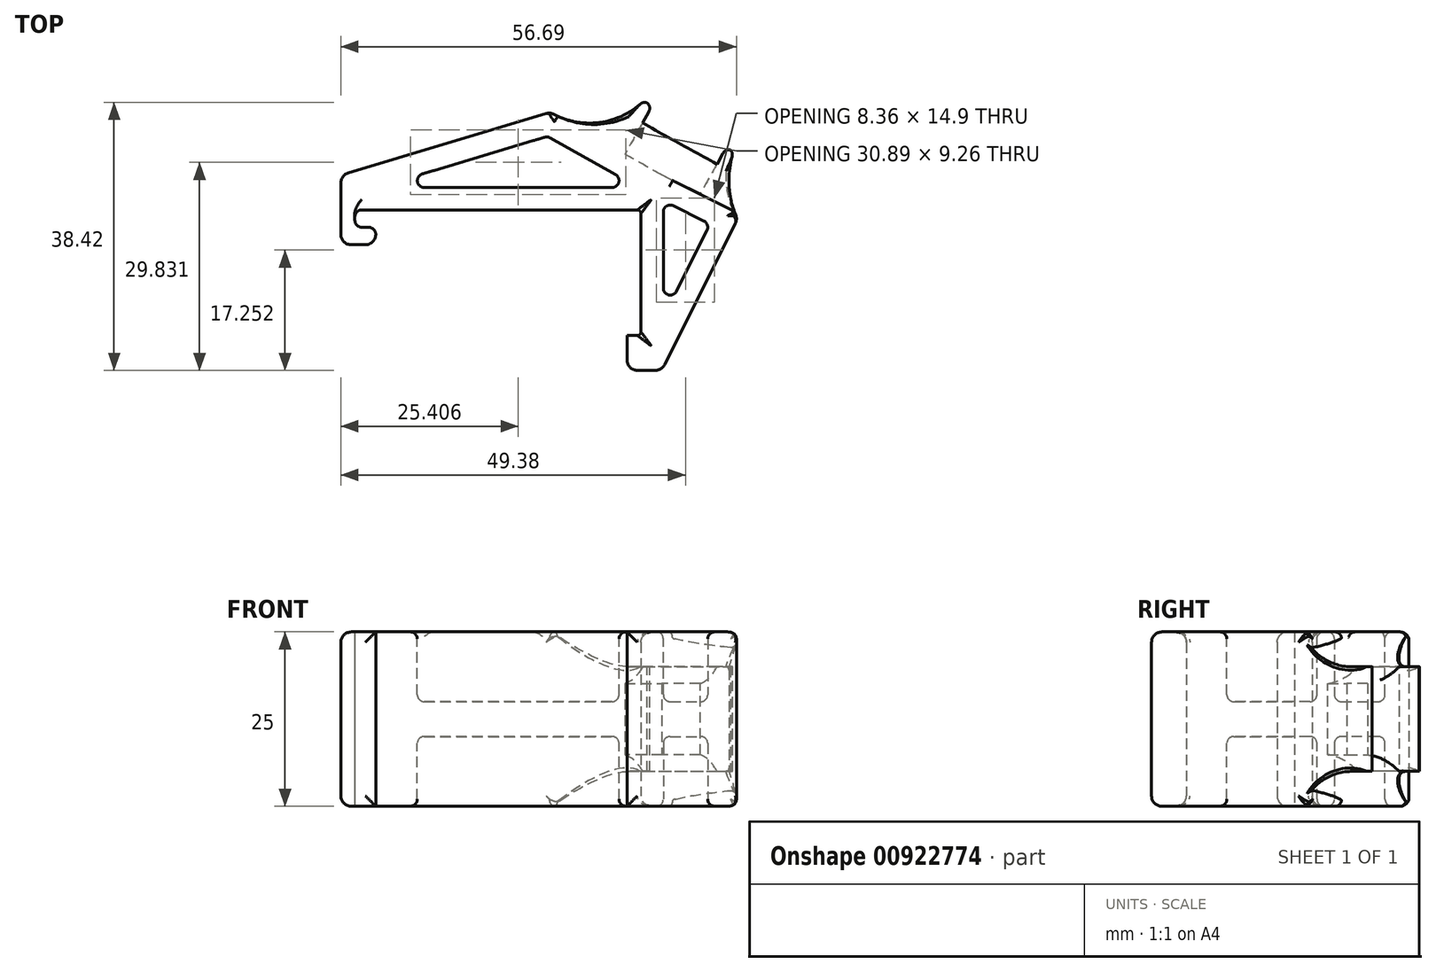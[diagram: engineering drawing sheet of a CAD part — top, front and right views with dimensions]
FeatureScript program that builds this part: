
annotation { "Feature Type Name" : "Feature", "Feature Type Description" : "" }
export const myFeature = defineFeature(function(context is Context, id is Id, definition is map)
    precondition{}
    {
        {
            var Q0;
            Q0=qCreatedBy(makeId("Top.planeOp"),FACE);
            var sketch = newSketch(context, id + "F0", { "sketchPlane" : qUnion([Q0])});
            skLineSegment(sketch, "E0.bottom", {"start": v(0, 0) * mm, "end": v(41, 0) * mm});
            skLineSegment(sketch, "E0.top", {"start": v(0, 2) * mm, "end": v(41, 2) * mm});
            skLineSegment(sketch, "E0.left", {"start": v(0, 0) * mm, "end": v(0, 2) * mm});
            skLineSegment(sketch, "E0.right", {"start": v(41, 0) * mm, "end": v(41, 2) * mm});
            skLineSegment(sketch, "E1.bottom", {"start": v(0, 2) * mm, "end": v(-2, 2) * mm});
            skLineSegment(sketch, "E1.top", {"start": v(0, -2.5) * mm, "end": v(-2, -2.5) * mm});
            skLineSegment(sketch, "E1.left", {"start": v(0, 2) * mm, "end": v(0, -2.5) * mm});
            skLineSegment(sketch, "E1.right", {"start": v(-2, 2) * mm, "end": v(-2, -2.5) * mm});
            skLineSegment(sketch, "E2.bottom", {"start": v(-2, -2.5) * mm, "end": v(3, -2.5) * mm});
            skLineSegment(sketch, "E2.top", {"start": v(-2, -5) * mm, "end": v(3, -5) * mm});
            skLineSegment(sketch, "E2.left", {"start": v(-2, -2.5) * mm, "end": v(-2, -5) * mm});
            skLineSegment(sketch, "E2.right", {"start": v(3, -2.5) * mm, "end": v(3, -5) * mm});
            skLineSegment(sketch, "E3.bottom", {"start": v(41, 2) * mm, "end": v(44, 2) * mm});
            skLineSegment(sketch, "E3.top", {"start": v(41, -23) * mm, "end": v(44, -23) * mm});
            skLineSegment(sketch, "E3.left", {"start": v(41, 2) * mm, "end": v(41, -23) * mm});
            skLineSegment(sketch, "E3.right", {"start": v(44, 2) * mm, "end": v(44, -23) * mm});
            skLineSegment(sketch, "E4.bottom", {"start": v(41, -23) * mm, "end": v(39, -23) * mm});
            skLineSegment(sketch, "E4.top", {"start": v(41, -18) * mm, "end": v(39, -18) * mm});
            skLineSegment(sketch, "E4.left", {"start": v(41, -23) * mm, "end": v(41, -18) * mm});
            skLineSegment(sketch, "E4.right", {"start": v(39, -23) * mm, "end": v(39, -18) * mm});
            skLineSegment(sketch, "E5.bottom", {"start": v(39, -23) * mm, "end": v(37.5, -23) * mm});
            skLineSegment(sketch, "E5.top", {"start": v(39, -13) * mm, "end": v(37.5, -13) * mm});
            skLineSegment(sketch, "E5.left", {"start": v(39, -23) * mm, "end": v(39, -13) * mm});
            skLineSegment(sketch, "E5.right", {"start": v(37.5, -23) * mm, "end": v(37.5, -13) * mm});
            skLineSegment(sketch, "E6.bottom", {"start": v(-2, 2) * mm, "end": v(44, 2) * mm});
            skLineSegment(sketch, "E6.top", {"start": v(-2, 5) * mm, "end": v(44, 5) * mm});
            skLineSegment(sketch, "E6.left", {"start": v(-2, 2) * mm, "end": v(-2, 5) * mm});
            skLineSegment(sketch, "E6.right", {"start": v(44, 2) * mm, "end": v(44, 5) * mm});
            skLineSegment(sketch, "E7", {"start": v(44, 5) * mm, "end": v(28, 14) * mm});
            skLineSegment(sketch, "E8", {"start": v(28, 14) * mm, "end": v(-2, 5) * mm});
            skLineSegment(sketch, "E9", {"start": v(28, 14) * mm, "end": v(28, 5) * mm});
            skLineSegment(sketch, "E10.bottom", {"start": v(37.5, -23) * mm, "end": v(39, -23) * mm});
            skLineSegment(sketch, "E10.top", {"start": v(37.5, -18) * mm, "end": v(39, -18) * mm});
            skLineSegment(sketch, "E10.left", {"start": v(37.5, -23) * mm, "end": v(37.5, -18) * mm});
            skLineSegment(sketch, "E11.bottom", {"start": v(44, 5) * mm, "end": v(28, 5) * mm});
            skLineSegment(sketch, "E11.top", {"start": v(44, 14) * mm, "end": v(28, 14) * mm});
            skLineSegment(sketch, "E11.left", {"start": v(44, 5) * mm, "end": v(44, 14) * mm});
            skLineSegment(sketch, "E11.right", {"start": v(28, 5) * mm, "end": v(28, 14) * mm});
            skLineSegment(sketch, "E12.bottom", {"start": v(-2, 5) * mm, "end": v(28, 5) * mm});
            skLineSegment(sketch, "E12.top", {"start": v(-2, 14) * mm, "end": v(28, 14) * mm});
            skLineSegment(sketch, "E12.left", {"start": v(-2, 5) * mm, "end": v(-2, 14) * mm});
            skLineSegment(sketch, "E13.bottom", {"start": v(44, 5) * mm, "end": v(62, 5) * mm});
            skLineSegment(sketch, "E13.top", {"start": v(44, -4) * mm, "end": v(62, -4) * mm});
            skLineSegment(sketch, "E13.left", {"start": v(44, 5) * mm, "end": v(44, -4) * mm});
            skLineSegment(sketch, "E13.right", {"start": v(62, 5) * mm, "end": v(62, -4) * mm});
            skLineSegment(sketch, "E14", {"start": v(44, 5) * mm, "end": v(62, -4) * mm});
            skLineSegment(sketch, "E15", {"start": v(62, -4) * mm, "end": v(44, -23) * mm});
            skLineSegment(sketch, "E16", {"start": v(44, -23) * mm, "end": v(55.2, -0.6) * mm});
            skSolve(sketch);
        }
        {
            var Q0;
            Q0=makeQuery(id+"F0.imprint","IMPRINT",FACE,{"disambiguationData":[TD([[makeQuery(id+"F0.imprint","IMPRINT",EDGE,{"derivedFrom":sQuery(id+"F0.wireOp",EDGE,"E2.top")}),1.0]])]});
            var Q1;
            Q1=makeQuery(id+"F0.imprint","IMPRINT",FACE,{"disambiguationData":[TD([[makeQuery(id+"F0.imprint","IMPRINT",EDGE,{"derivedFrom":sQuery(id+"F0.wireOp",EDGE,"E4.bottom")}),-1.0]])]});
            var Q2;
            Q2=makeQuery(id+"F0.imprint","IMPRINT",FACE,{"disambiguationData":[TD([[makeQuery(id+"F0.imprint","IMPRINT",EDGE,{"derivedFrom":sQuery(id+"F0.wireOp",EDGE,"E10.bottom")}),1.0]])]});
            var Q3;
            {var subQ0=sQuery(id+"F0.wireOp",EDGE,"E6.left");Q3=makeQuery(id+"F0.imprint","IMPRINT",FACE,{"disambiguationData":[TD([[makeQuery(id+"F0.imprint","IMPRINT",EDGE,{"derivedFrom":subQ0}),-1.0]])]});}
            var Q4;
            Q4=makeQuery(id+"F0.imprint","IMPRINT",FACE,{"disambiguationData":[TD([[makeQuery(id+"F0.imprint","IMPRINT",EDGE,{"derivedFrom":sQuery(id+"F0.wireOp",EDGE,"E3.right")}),1.0]])]});
            var Q5;
            Q5=makeQuery(id+"F0.imprint","IMPRINT",FACE,{"disambiguationData":[TD([[makeQuery(id+"F0.imprint","IMPRINT",EDGE,{"derivedFrom":sQuery(id+"F0.wireOp",EDGE,"E3.top")}),1.0]])]});
            var Q6;
            {var subQ4=sQuery(id+"F0.wireOp",EDGE,"E14");var subQ6=sQuery(id+"F0.wireOp",EDGE,"E16");var subQ7=makeQuery(id+"F0.imprint","INTERSECT",VERTEX,{"derivedFrom":[subQ4,subQ6]});Q6=makeQuery(id+"F0.imprint","IMPRINT",FACE,{"disambiguationData":[TD([[makeQuery(id+"F0.imprint","IMPRINT",EDGE,{"disambiguationData":[TD([[subQ7,1.0]])],"derivedFrom":subQ6}),1.0]])]});}
            var Q7;
            Q7=makeQuery(id+"F0.imprint","IMPRINT",FACE,{"disambiguationData":[TD([[makeQuery(id+"F0.imprint","IMPRINT",EDGE,{"derivedFrom":sQuery(id+"F0.wireOp",EDGE,"E8")}),1.0]])]});
            var Q8;
            {var subQ3=sQuery(id+"F0.wireOp",EDGE,"E1.right");Q8=makeQuery(id+"F0.imprint","IMPRINT",FACE,{"disambiguationData":[TD([[makeQuery(id+"F0.imprint","IMPRINT",EDGE,{"derivedFrom":subQ3}),1.0]])]});}
            var Q9;
            Q9=makeQuery(id+"F0.imprint","IMPRINT",FACE,{"disambiguationData":[TD([[makeQuery(id+"F0.imprint","IMPRINT",EDGE,{"derivedFrom":sQuery(id+"F0.wireOp",EDGE,"E7")}),1.0]])]});
            var Q10;
            {var subQ0=sQuery(id+"F0.wireOp",EDGE,"E0.bottom");Q10=makeQuery(id+"F0.imprint","IMPRINT",FACE,{"disambiguationData":[TD([[makeQuery(id+"F0.imprint","IMPRINT",EDGE,{"derivedFrom":subQ0}),1.0]])]});}
            extrude(context, id + "F1", {"entities" : qUnion([Q0, Q1, Q2, Q3, Q4, Q5, Q6, Q7, Q8, Q9, Q10]), "depth" : 12.5 * mm, "offsetDistance" : 25 * mm, "hasSecondDirection" : true, "secondDirectionOppositeDirection" : true, "secondDirectionDepth" : 12.5 * mm});
        }
        {
            var Q0;
            Q0=makeQuery(id+"F1.opExtrude","CAP_FACE",FACE,{"disambiguationData":[OSD([sQuery(id+"F0.wireOp",EDGE,"E1.left"),sQuery(id+"F0.wireOp",EDGE,"E1.right"),sQuery(id+"F0.wireOp",EDGE,"E2.bottom"),sQuery(id+"F0.wireOp",EDGE,"E2.top"),sQuery(id+"F0.wireOp",EDGE,"E2.left"),sQuery(id+"F0.wireOp",EDGE,"E2.right"),sQuery(id+"F0.wireOp",EDGE,"E3.top"),sQuery(id+"F0.wireOp",EDGE,"E3.left"),sQuery(id+"F0.wireOp",EDGE,"E4.bottom"),sQuery(id+"F0.wireOp",EDGE,"E4.top"),sQuery(id+"F0.wireOp",EDGE,"E6.bottom"),sQuery(id+"F0.wireOp",EDGE,"E6.left"),sQuery(id+"F0.wireOp",EDGE,"E7"),sQuery(id+"F0.wireOp",EDGE,"E8"),sQuery(id+"F0.wireOp",EDGE,"E10.bottom"),sQuery(id+"F0.wireOp",EDGE,"E10.top"),sQuery(id+"F0.wireOp",EDGE,"E10.left"),sQuery(id+"F0.wireOp",EDGE,"E14"),sQuery(id+"F0.wireOp",EDGE,"E16")])],"isStart":false});
            var Q1;
            Q1=makeQuery(id+"F1.opExtrude","CAP_FACE",FACE,{"disambiguationData":[OSD([sQuery(id+"F0.wireOp",EDGE,"E1.left"),sQuery(id+"F0.wireOp",EDGE,"E1.right"),sQuery(id+"F0.wireOp",EDGE,"E2.bottom"),sQuery(id+"F0.wireOp",EDGE,"E2.top"),sQuery(id+"F0.wireOp",EDGE,"E2.left"),sQuery(id+"F0.wireOp",EDGE,"E2.right"),sQuery(id+"F0.wireOp",EDGE,"E3.top"),sQuery(id+"F0.wireOp",EDGE,"E3.left"),sQuery(id+"F0.wireOp",EDGE,"E4.bottom"),sQuery(id+"F0.wireOp",EDGE,"E4.top"),sQuery(id+"F0.wireOp",EDGE,"E6.bottom"),sQuery(id+"F0.wireOp",EDGE,"E6.left"),sQuery(id+"F0.wireOp",EDGE,"E7"),sQuery(id+"F0.wireOp",EDGE,"E8"),sQuery(id+"F0.wireOp",EDGE,"E10.bottom"),sQuery(id+"F0.wireOp",EDGE,"E10.top"),sQuery(id+"F0.wireOp",EDGE,"E10.left"),sQuery(id+"F0.wireOp",EDGE,"E14"),sQuery(id+"F0.wireOp",EDGE,"E16")])],"isStart":true});
            shell(context, id + "F2", {"entities" : qUnion([Q0, Q1]), "thickness" : 3.2 * mm});
        }
        {
            var Q0;
            Q0=makeQuery(id+"F1.opExtrude","SWEPT_FACE",FACE,{"disambiguationData":[OSD([sQuery(id+"F0.wireOp",EDGE,"E7"),sQuery(id+"F0.wireOp",EDGE,"E14")])]});
            var sketch = newSketch(context, id + "F3", { "sketchPlane" : qUnion([Q0])});
            skLineSegment(sketch, "E17", {"start": v(-17.54, 0) * mm, "end": v(-48.4, 0) * mm});
            skLineSegment(sketch, "E18", {"start": v(-35.9, 0) * mm, "end": v(-35.9, 12.5) * mm});
            skLineSegment(sketch, "E19.bottom", {"start": v(-29.8, 5.1) * mm, "end": v(-42, 5.1) * mm});
            skLineSegment(sketch, "E19.top", {"start": v(-29.8, -5.1) * mm, "end": v(-42, -5.1) * mm});
            skLineSegment(sketch, "E19.left", {"start": v(-29.8, 5.1) * mm, "end": v(-29.8, -5.1) * mm});
            skLineSegment(sketch, "E19.right", {"start": v(-42, 5.1) * mm, "end": v(-42, -5.1) * mm});
            skPoint(sketch, "E19.middle", {"position": v(-35.9, 0) * mm});
            skLineSegment(sketch, "E20.bottom", {"start": v(-28.4, 7.5) * mm, "end": v(-43.4, 7.5) * mm});
            skLineSegment(sketch, "E20.top", {"start": v(-28.4, -7.5) * mm, "end": v(-43.4, -7.5) * mm});
            skLineSegment(sketch, "E20.left", {"start": v(-28.4, 7.5) * mm, "end": v(-28.4, -7.5) * mm});
            skLineSegment(sketch, "E20.right", {"start": v(-43.4, 7.5) * mm, "end": v(-43.4, -7.5) * mm});
            skSolve(sketch);
        }
        {
            var Q0;
            Q0 = qSketchRegion(id + "F3", true);
            extrude(context, id + "F4", {"entities" : qUnion([Q0]), "operationType" : NewBodyOperationType.ADD, "depth" : 8 * mm, "offsetDistance" : 25 * mm});
        }
        {
            var Q0;
            Q0=makeQuery(id+"F4.opExtrude","CAP_EDGE",EDGE,{"disambiguationData":[OSD([sQuery(id+"F3.wireOp",EDGE,"E19.bottom")])],"isStart":false});
            var Q1;
            Q1=makeQuery(id+"F4.opExtrude","CAP_EDGE",EDGE,{"disambiguationData":[OSD([sQuery(id+"F3.wireOp",EDGE,"E19.top")])],"isStart":false});
            fillet(context, id + "F5", {"entities" : qUnion([Q0, Q1]), "radius" : 9 * mm, "tangentPropagation" : true, "allowEdgeOverflow" : false});
        }
        {
            var Q0;
            Q0=makeQuery(id+"F4.opExtrude","CAP_EDGE",EDGE,{"disambiguationData":[OSD([sQuery(id+"F3.wireOp",EDGE,"E20.bottom")])],"isStart":true});
            var Q1;
            Q1=makeQuery(id+"F4.opExtrude","CAP_EDGE",EDGE,{"disambiguationData":[OSD([sQuery(id+"F3.wireOp",EDGE,"E20.top")])],"isStart":true});
            var Q2;
            Q2=makeQuery(id+"F4.opExtrude","CAP_EDGE",EDGE,{"disambiguationData":[OSD([sQuery(id+"F3.wireOp",EDGE,"E20.right")])],"isStart":true});
            fillet(context, id + "F6", {"entities" : qUnion([Q0, Q1, Q2]), "radius" : 5 * mm, "tangentPropagation" : true, "allowEdgeOverflow" : false});
        }
        {
            var Q0;
            Q0=makeQuery(id+"F4.opExtrude","CAP_EDGE",EDGE,{"disambiguationData":[OSD([sQuery(id+"F3.wireOp",EDGE,"E20.left")])],"isStart":true});
            fillet(context, id + "F7", {"entities" : qUnion([Q0]), "radius" : 11 * mm, "tangentPropagation" : true, "allowEdgeOverflow" : false});
        }
        {
            var Q0;
            {var subQ0=sQuery(id+"F0.wireOp",EDGE,"E6.left");Q0=makeQuery(id+"F0.imprint","IMPRINT",FACE,{"disambiguationData":[TD([[makeQuery(id+"F0.imprint","IMPRINT",EDGE,{"derivedFrom":subQ0}),-1.0]])]});}
            var Q1;
            Q1=makeQuery(id+"F0.imprint","IMPRINT",FACE,{"disambiguationData":[TD([[makeQuery(id+"F0.imprint","IMPRINT",EDGE,{"derivedFrom":sQuery(id+"F0.wireOp",EDGE,"E7")}),1.0]])]});
            var Q2;
            Q2=makeQuery(id+"F0.imprint","IMPRINT",FACE,{"disambiguationData":[TD([[makeQuery(id+"F0.imprint","IMPRINT",EDGE,{"derivedFrom":sQuery(id+"F0.wireOp",EDGE,"E8")}),1.0]])]});
            var Q3;
            {var subQ4=sQuery(id+"F0.wireOp",EDGE,"E14");var subQ6=sQuery(id+"F0.wireOp",EDGE,"E16");var subQ7=makeQuery(id+"F0.imprint","INTERSECT",VERTEX,{"derivedFrom":[subQ4,subQ6]});Q3=makeQuery(id+"F0.imprint","IMPRINT",FACE,{"disambiguationData":[TD([[makeQuery(id+"F0.imprint","IMPRINT",EDGE,{"disambiguationData":[TD([[subQ7,1.0]])],"derivedFrom":subQ6}),1.0]])]});}
            var Q4;
            {var subQ0=sQuery(id+"F0.wireOp",EDGE,"E3.right");Q4=makeQuery(id+"F0.imprint","IMPRINT",FACE,{"disambiguationData":[TD([[makeQuery(id+"F0.imprint","IMPRINT",EDGE,{"derivedFrom":subQ0}),1.0]])]});}
            extrude(context, id + "F8", {"entities" : qUnion([Q0, Q1, Q2, Q3, Q4]), "operationType" : NewBodyOperationType.ADD, "depth" : 2.5 * mm, "offsetDistance" : 25 * mm, "hasSecondDirection" : true, "secondDirectionOppositeDirection" : true, "secondDirectionDepth" : 2.5 * mm});
        }
        {
            var Q0;
            Q0=makeQuery(id+"F1.opExtrude","SWEPT_FACE",FACE,{"disambiguationData":[OSD([sQuery(id+"F0.wireOp",EDGE,"E1.right"),sQuery(id+"F0.wireOp",EDGE,"E2.left"),sQuery(id+"F0.wireOp",EDGE,"E6.left")])]});
            var Q1;
            Q1=makeQuery(id+"F1.opExtrude","SWEPT_FACE",FACE,{"disambiguationData":[OSD([sQuery(id+"F0.wireOp",EDGE,"E2.top")])]});
            var Q2;
            Q2=makeQuery(id+"F1.opExtrude","SWEPT_FACE",FACE,{"disambiguationData":[OSD([sQuery(id+"F0.wireOp",EDGE,"E8")])]});
            var Q3;
            Q3=makeQuery(id+"F1.opExtrude","SWEPT_FACE",FACE,{"disambiguationData":[OSD([sQuery(id+"F0.wireOp",EDGE,"E16")])]});
            var Q4;
            Q4=makeQuery(id+"F1.opExtrude","SWEPT_FACE",FACE,{"disambiguationData":[OSD([sQuery(id+"F0.wireOp",EDGE,"E3.top"),sQuery(id+"F0.wireOp",EDGE,"E4.bottom"),sQuery(id+"F0.wireOp",EDGE,"E10.bottom")])]});
            var Q5;
            Q5=makeQuery(id+"F1.opExtrude","SWEPT_FACE",FACE,{"disambiguationData":[OSD([sQuery(id+"F0.wireOp",EDGE,"E10.left")])]});
            var Q6;
            Q6=makeQuery(id+"F1.opExtrude","CAP_EDGE",EDGE,{"disambiguationData":[OSD([sQuery(id+"F0.wireOp",EDGE,"E4.top"),sQuery(id+"F0.wireOp",EDGE,"E10.top")])],"isStart":false});
            var Q7;
            Q7=makeQuery(id+"F1.opExtrude","CAP_EDGE",EDGE,{"disambiguationData":[OSD([sQuery(id+"F0.wireOp",EDGE,"E3.left")])],"isStart":false});
            var Q8;
            Q8=makeQuery(id+"F1.opExtrude","CAP_EDGE",EDGE,{"disambiguationData":[OSD([sQuery(id+"F0.wireOp",EDGE,"E0.bottom")])],"isStart":false});
            var Q9;
            Q9=makeQuery(id+"F1.opExtrude","CAP_EDGE",EDGE,{"disambiguationData":[OSD([sQuery(id+"F0.wireOp",EDGE,"E4.top"),sQuery(id+"F0.wireOp",EDGE,"E10.top")])],"isStart":true});
            var Q10;
            Q10=makeQuery(id+"F1.opExtrude","CAP_EDGE",EDGE,{"disambiguationData":[OSD([sQuery(id+"F0.wireOp",EDGE,"E3.left")])],"isStart":true});
            var Q11;
            Q11=makeQuery(id+"F1.opExtrude","CAP_EDGE",EDGE,{"disambiguationData":[OSD([sQuery(id+"F0.wireOp",EDGE,"E0.bottom")])],"isStart":true});
            fillet(context, id + "F9", {"entities" : qUnion([Q0, Q1, Q2, Q3, Q4, Q5, Q6, Q7, Q8, Q9, Q10, Q11]), "radius" : 1.5 * mm, "tangentPropagation" : true, "allowEdgeOverflow" : false});
        }
        {
            var Q0;
            {var subQ0=sQuery(id+"F0.wireOp",EDGE,"E14");var subQ1=sQuery(id+"F0.wireOp",EDGE,"E7");Q0=makeQuery(id+"F7.opFillet","MERGE",EDGE,{"derivedFrom":[makeQuery(id+"F6.opFillet","BLEND_EDGE",EDGE,{"blendedFrom":[makeQuery(id+"F4.opExtrude","CAP_EDGE",EDGE,{"disambiguationData":[OSD([sQuery(id+"F3.wireOp",EDGE,"E20.top")])],"isStart":true}),makeQuery(id+"F1.opExtrude","CAP_FACE",FACE,{"disambiguationData":[OSD([sQuery(id+"F0.wireOp",EDGE,"E1.left"),sQuery(id+"F0.wireOp",EDGE,"E1.right"),sQuery(id+"F0.wireOp",EDGE,"E2.bottom"),sQuery(id+"F0.wireOp",EDGE,"E2.top"),sQuery(id+"F0.wireOp",EDGE,"E2.left"),sQuery(id+"F0.wireOp",EDGE,"E2.right"),sQuery(id+"F0.wireOp",EDGE,"E3.top"),sQuery(id+"F0.wireOp",EDGE,"E3.left"),sQuery(id+"F0.wireOp",EDGE,"E4.bottom"),sQuery(id+"F0.wireOp",EDGE,"E4.top"),sQuery(id+"F0.wireOp",EDGE,"E6.bottom"),sQuery(id+"F0.wireOp",EDGE,"E6.left"),subQ1,sQuery(id+"F0.wireOp",EDGE,"E8"),sQuery(id+"F0.wireOp",EDGE,"E10.bottom"),sQuery(id+"F0.wireOp",EDGE,"E10.top"),sQuery(id+"F0.wireOp",EDGE,"E10.left"),subQ0,sQuery(id+"F0.wireOp",EDGE,"E16")])],"isStart":true})],"blendedInto":[makeQuery(id+"F1.opExtrude","CAP_FACE",FACE,{"disambiguationData":[OSD([sQuery(id+"F0.wireOp",EDGE,"E1.left"),sQuery(id+"F0.wireOp",EDGE,"E1.right"),sQuery(id+"F0.wireOp",EDGE,"E2.bottom"),sQuery(id+"F0.wireOp",EDGE,"E2.top"),sQuery(id+"F0.wireOp",EDGE,"E2.left"),sQuery(id+"F0.wireOp",EDGE,"E2.right"),sQuery(id+"F0.wireOp",EDGE,"E3.top"),sQuery(id+"F0.wireOp",EDGE,"E3.left"),sQuery(id+"F0.wireOp",EDGE,"E4.bottom"),sQuery(id+"F0.wireOp",EDGE,"E4.top"),sQuery(id+"F0.wireOp",EDGE,"E6.bottom"),sQuery(id+"F0.wireOp",EDGE,"E6.left"),subQ1,sQuery(id+"F0.wireOp",EDGE,"E8"),sQuery(id+"F0.wireOp",EDGE,"E10.bottom"),sQuery(id+"F0.wireOp",EDGE,"E10.top"),sQuery(id+"F0.wireOp",EDGE,"E10.left"),subQ0,sQuery(id+"F0.wireOp",EDGE,"E16")])],"isStart":true})]}),makeQuery(id+"F1.opExtrude","CAP_EDGE",EDGE,{"disambiguationData":[OSD([subQ1,subQ0])],"isStart":true})]});}
            var Q1;
            {var subQ0=sQuery(id+"F0.wireOp",EDGE,"E14");var subQ1=sQuery(id+"F0.wireOp",EDGE,"E7");Q1=makeQuery(id+"F7.opFillet","MERGE",EDGE,{"derivedFrom":[makeQuery(id+"F6.opFillet","BLEND_EDGE",EDGE,{"blendedFrom":[makeQuery(id+"F4.opExtrude","CAP_EDGE",EDGE,{"disambiguationData":[OSD([sQuery(id+"F3.wireOp",EDGE,"E20.bottom")])],"isStart":true}),makeQuery(id+"F1.opExtrude","CAP_FACE",FACE,{"disambiguationData":[OSD([sQuery(id+"F0.wireOp",EDGE,"E1.left"),sQuery(id+"F0.wireOp",EDGE,"E1.right"),sQuery(id+"F0.wireOp",EDGE,"E2.bottom"),sQuery(id+"F0.wireOp",EDGE,"E2.top"),sQuery(id+"F0.wireOp",EDGE,"E2.left"),sQuery(id+"F0.wireOp",EDGE,"E2.right"),sQuery(id+"F0.wireOp",EDGE,"E3.top"),sQuery(id+"F0.wireOp",EDGE,"E3.left"),sQuery(id+"F0.wireOp",EDGE,"E4.bottom"),sQuery(id+"F0.wireOp",EDGE,"E4.top"),sQuery(id+"F0.wireOp",EDGE,"E6.bottom"),sQuery(id+"F0.wireOp",EDGE,"E6.left"),subQ1,sQuery(id+"F0.wireOp",EDGE,"E8"),sQuery(id+"F0.wireOp",EDGE,"E10.bottom"),sQuery(id+"F0.wireOp",EDGE,"E10.top"),sQuery(id+"F0.wireOp",EDGE,"E10.left"),subQ0,sQuery(id+"F0.wireOp",EDGE,"E16")])],"isStart":false})],"blendedInto":[makeQuery(id+"F1.opExtrude","CAP_FACE",FACE,{"disambiguationData":[OSD([sQuery(id+"F0.wireOp",EDGE,"E1.left"),sQuery(id+"F0.wireOp",EDGE,"E1.right"),sQuery(id+"F0.wireOp",EDGE,"E2.bottom"),sQuery(id+"F0.wireOp",EDGE,"E2.top"),sQuery(id+"F0.wireOp",EDGE,"E2.left"),sQuery(id+"F0.wireOp",EDGE,"E2.right"),sQuery(id+"F0.wireOp",EDGE,"E3.top"),sQuery(id+"F0.wireOp",EDGE,"E3.left"),sQuery(id+"F0.wireOp",EDGE,"E4.bottom"),sQuery(id+"F0.wireOp",EDGE,"E4.top"),sQuery(id+"F0.wireOp",EDGE,"E6.bottom"),sQuery(id+"F0.wireOp",EDGE,"E6.left"),subQ1,sQuery(id+"F0.wireOp",EDGE,"E8"),sQuery(id+"F0.wireOp",EDGE,"E10.bottom"),sQuery(id+"F0.wireOp",EDGE,"E10.top"),sQuery(id+"F0.wireOp",EDGE,"E10.left"),subQ0,sQuery(id+"F0.wireOp",EDGE,"E16")])],"isStart":false})]}),makeQuery(id+"F1.opExtrude","CAP_EDGE",EDGE,{"disambiguationData":[OSD([subQ1,subQ0])],"isStart":false})]});}
            var Q2;
            Q2=makeQuery(id+"F1.opExtrude","SWEPT_EDGE",EDGE,{"disambiguationData":[OSD([sQuery(id+"F0.wireOp",EDGE,"E1.left"),sQuery(id+"F0.wireOp",EDGE,"E2.bottom")])]});
            var Q3;
            Q3=makeQuery(id+"F1.opExtrude","SWEPT_EDGE",EDGE,{"disambiguationData":[OSD([sQuery(id+"F0.wireOp",EDGE,"E2.bottom"),sQuery(id+"F0.wireOp",EDGE,"E2.right")])]});
            var Q4;
            Q4=makeQuery(id+"F1.opExtrude","SWEPT_EDGE",EDGE,{"disambiguationData":[OSD([sQuery(id+"F0.wireOp",EDGE,"E1.left"),sQuery(id+"F0.wireOp",EDGE,"E6.bottom")])]});
            fillet(context, id + "F10", {"entities" : qUnion([Q0, Q1, Q2, Q3, Q4]), "radius" : 1 * mm, "tangentPropagation" : true, "allowEdgeOverflow" : false});
        }
        {
            var Q0;
            Q0=makeQuery(id+"F8.opExtrude","CAP_FACE",FACE,{"disambiguationData":[OSD([sQuery(id+"F0.wireOp",EDGE,"E6.bottom"),sQuery(id+"F0.wireOp",EDGE,"E6.left"),sQuery(id+"F0.wireOp",EDGE,"E7"),sQuery(id+"F0.wireOp",EDGE,"E8"),sQuery(id+"F0.wireOp",EDGE,"E13.left")])],"isStart":false});
            var Q1;
            Q1=makeQuery(id+"F8.opExtrude","CAP_FACE",FACE,{"disambiguationData":[OSD([sQuery(id+"F0.wireOp",EDGE,"E6.bottom"),sQuery(id+"F0.wireOp",EDGE,"E6.left"),sQuery(id+"F0.wireOp",EDGE,"E7"),sQuery(id+"F0.wireOp",EDGE,"E8"),sQuery(id+"F0.wireOp",EDGE,"E13.left")])],"isStart":true});
            var Q2;
            {var subQ0=sQuery(id+"F0.wireOp",EDGE,"E14");var subQ1=sQuery(id+"F0.wireOp",EDGE,"E8");var subQ2=sQuery(id+"F0.wireOp",EDGE,"E7");var subQ3=sQuery(id+"F0.wireOp",EDGE,"E6.left");var subQ4=sQuery(id+"F0.wireOp",EDGE,"E0.bottom");Q2=makeQuery(id+"F8.boolean.opBoolean","SPLIT",EDGE,{"disambiguationData":[TD([makeQuery(id+"F8.opExtrude","CAP_FACE",FACE,{"disambiguationData":[OSD([sQuery(id+"F0.wireOp",EDGE,"E6.bottom"),subQ3,subQ2,subQ1,sQuery(id+"F0.wireOp",EDGE,"E13.left")])],"isStart":true})])],"derivedFrom":makeQuery(id+"F2.opShell","TWEAK_EDGE",EDGE,{"derivedFrom":[makeQuery(id+"F1.opExtrude","SWEPT_FACE",FACE,{"disambiguationData":[OSD([subQ4])]}),makeQuery(id+"F1.opExtrude","SWEPT_FACE",FACE,{"disambiguationData":[OSD([subQ2,subQ0])]})]})});}
            var Q3;
            {var subQ1=sQuery(id+"F0.wireOp",EDGE,"E8");var subQ2=sQuery(id+"F0.wireOp",EDGE,"E7");var subQ3=sQuery(id+"F0.wireOp",EDGE,"E6.left");Q3=makeQuery(id+"F8.boolean.opBoolean","SPLIT",EDGE,{"disambiguationData":[TD([makeQuery(id+"F8.opExtrude","CAP_FACE",FACE,{"disambiguationData":[OSD([sQuery(id+"F0.wireOp",EDGE,"E6.bottom"),subQ3,subQ2,subQ1,sQuery(id+"F0.wireOp",EDGE,"E13.left")])],"isStart":true})])],"derivedFrom":makeQuery(id+"F2.opShell","OFFSET_EDGE",EDGE,{"disambiguationData":[OSD([subQ2,subQ1,sQuery(id+"F0.wireOp",EDGE,"E11.top"),sQuery(id+"F0.wireOp",EDGE,"E12.top"),sQuery(id+"F0.wireOp",EDGE,"E11.right")])]})});}
            var Q4;
            {var subQ0=sQuery(id+"F0.wireOp",EDGE,"E8");var subQ1=sQuery(id+"F0.wireOp",EDGE,"E7");var subQ2=sQuery(id+"F0.wireOp",EDGE,"E6.left");var subQ3=sQuery(id+"F0.wireOp",EDGE,"E0.bottom");Q4=makeQuery(id+"F8.boolean.opBoolean","SPLIT",EDGE,{"disambiguationData":[TD([makeQuery(id+"F8.opExtrude","CAP_FACE",FACE,{"disambiguationData":[OSD([sQuery(id+"F0.wireOp",EDGE,"E6.bottom"),subQ2,subQ1,subQ0,sQuery(id+"F0.wireOp",EDGE,"E13.left")])],"isStart":true})])],"derivedFrom":makeQuery(id+"F2.opShell","TWEAK_EDGE",EDGE,{"derivedFrom":[makeQuery(id+"F1.opExtrude","SWEPT_FACE",FACE,{"disambiguationData":[OSD([subQ3])]}),makeQuery(id+"F1.opExtrude","SWEPT_FACE",FACE,{"disambiguationData":[OSD([subQ0])]})]})});}
            var Q5;
            {var subQ0=sQuery(id+"F0.wireOp",EDGE,"E0.bottom");Q5=makeQuery(id+"F2.opShell","OFFSET_EDGE",EDGE,{"disambiguationData":[OSD([subQ0]),TDD([makeQuery(id+"F1.opExtrude","CAP_EDGE",EDGE,{"disambiguationData":[OSD([subQ0])],"isStart":true})])]});}
            var Q6;
            {var subQ0=sQuery(id+"F0.wireOp",EDGE,"E14");var subQ1=sQuery(id+"F0.wireOp",EDGE,"E7");Q6=makeQuery(id+"F2.opShell","OFFSET_EDGE",EDGE,{"disambiguationData":[OSD([subQ1,subQ0]),TDD([makeQuery(id+"F1.opExtrude","CAP_EDGE",EDGE,{"disambiguationData":[OSD([subQ1,subQ0])],"isStart":true})]),OD(0.0)]});}
            var Q7;
            {var subQ0=sQuery(id+"F0.wireOp",EDGE,"E8");Q7=makeQuery(id+"F2.opShell","OFFSET_EDGE",EDGE,{"disambiguationData":[OSD([subQ0]),TDD([makeQuery(id+"F1.opExtrude","CAP_EDGE",EDGE,{"disambiguationData":[OSD([subQ0])],"isStart":true})])]});}
            var Q8;
            {var subQ0=sQuery(id+"F0.wireOp",EDGE,"E14");var subQ1=sQuery(id+"F0.wireOp",EDGE,"E8");var subQ2=sQuery(id+"F0.wireOp",EDGE,"E7");var subQ3=sQuery(id+"F0.wireOp",EDGE,"E6.left");var subQ4=sQuery(id+"F0.wireOp",EDGE,"E0.bottom");Q8=makeQuery(id+"F8.boolean.opBoolean","SPLIT",EDGE,{"disambiguationData":[TD([makeQuery(id+"F8.opExtrude","CAP_FACE",FACE,{"disambiguationData":[OSD([sQuery(id+"F0.wireOp",EDGE,"E6.bottom"),subQ3,subQ2,subQ1,sQuery(id+"F0.wireOp",EDGE,"E13.left")])],"isStart":false})])],"derivedFrom":makeQuery(id+"F2.opShell","TWEAK_EDGE",EDGE,{"derivedFrom":[makeQuery(id+"F1.opExtrude","SWEPT_FACE",FACE,{"disambiguationData":[OSD([subQ4])]}),makeQuery(id+"F1.opExtrude","SWEPT_FACE",FACE,{"disambiguationData":[OSD([subQ2,subQ0])]})]})});}
            var Q9;
            {var subQ1=sQuery(id+"F0.wireOp",EDGE,"E8");var subQ2=sQuery(id+"F0.wireOp",EDGE,"E7");var subQ3=sQuery(id+"F0.wireOp",EDGE,"E6.left");Q9=makeQuery(id+"F8.boolean.opBoolean","SPLIT",EDGE,{"disambiguationData":[TD([makeQuery(id+"F8.opExtrude","CAP_FACE",FACE,{"disambiguationData":[OSD([sQuery(id+"F0.wireOp",EDGE,"E6.bottom"),subQ3,subQ2,subQ1,sQuery(id+"F0.wireOp",EDGE,"E13.left")])],"isStart":false})])],"derivedFrom":makeQuery(id+"F2.opShell","OFFSET_EDGE",EDGE,{"disambiguationData":[OSD([subQ2,subQ1,sQuery(id+"F0.wireOp",EDGE,"E11.top"),sQuery(id+"F0.wireOp",EDGE,"E12.top"),sQuery(id+"F0.wireOp",EDGE,"E11.right")])]})});}
            var Q10;
            {var subQ0=sQuery(id+"F0.wireOp",EDGE,"E8");var subQ1=sQuery(id+"F0.wireOp",EDGE,"E7");var subQ2=sQuery(id+"F0.wireOp",EDGE,"E6.left");var subQ3=sQuery(id+"F0.wireOp",EDGE,"E0.bottom");Q10=makeQuery(id+"F8.boolean.opBoolean","SPLIT",EDGE,{"disambiguationData":[TD([makeQuery(id+"F8.opExtrude","CAP_FACE",FACE,{"disambiguationData":[OSD([sQuery(id+"F0.wireOp",EDGE,"E6.bottom"),subQ2,subQ1,subQ0,sQuery(id+"F0.wireOp",EDGE,"E13.left")])],"isStart":false})])],"derivedFrom":makeQuery(id+"F2.opShell","TWEAK_EDGE",EDGE,{"derivedFrom":[makeQuery(id+"F1.opExtrude","SWEPT_FACE",FACE,{"disambiguationData":[OSD([subQ3])]}),makeQuery(id+"F1.opExtrude","SWEPT_FACE",FACE,{"disambiguationData":[OSD([subQ0])]})]})});}
            var Q11;
            {var subQ0=sQuery(id+"F0.wireOp",EDGE,"E0.bottom");Q11=makeQuery(id+"F2.opShell","OFFSET_EDGE",EDGE,{"disambiguationData":[OSD([subQ0]),TDD([makeQuery(id+"F1.opExtrude","CAP_EDGE",EDGE,{"disambiguationData":[OSD([subQ0])],"isStart":false})])]});}
            var Q12;
            {var subQ0=sQuery(id+"F0.wireOp",EDGE,"E3.left");Q12=makeQuery(id+"F2.opShell","OFFSET_EDGE",EDGE,{"disambiguationData":[OSD([subQ0]),TDD([makeQuery(id+"F1.opExtrude","CAP_EDGE",EDGE,{"disambiguationData":[OSD([subQ0])],"isStart":true})])]});}
            var Q13;
            {var subQ0=sQuery(id+"F0.wireOp",EDGE,"E14");var subQ1=sQuery(id+"F0.wireOp",EDGE,"E7");Q13=makeQuery(id+"F2.opShell","OFFSET_EDGE",EDGE,{"disambiguationData":[OSD([subQ1,subQ0]),TDD([makeQuery(id+"F1.opExtrude","CAP_EDGE",EDGE,{"disambiguationData":[OSD([subQ1,subQ0])],"isStart":true})]),OD(1.0)]});}
            var Q14;
            {var subQ0=sQuery(id+"F0.wireOp",EDGE,"E16");Q14=makeQuery(id+"F2.opShell","OFFSET_EDGE",EDGE,{"disambiguationData":[OSD([subQ0]),TDD([makeQuery(id+"F1.opExtrude","CAP_EDGE",EDGE,{"disambiguationData":[OSD([subQ0])],"isStart":true})])]});}
            var Q15;
            {var subQ0=sQuery(id+"F0.wireOp",EDGE,"E3.left");Q15=makeQuery(id+"F2.opShell","OFFSET_EDGE",EDGE,{"disambiguationData":[OSD([subQ0]),TDD([makeQuery(id+"F1.opExtrude","CAP_EDGE",EDGE,{"disambiguationData":[OSD([subQ0])],"isStart":false})])]});}
            var Q16;
            {var subQ0=sQuery(id+"F0.wireOp",EDGE,"E14");var subQ1=sQuery(id+"F0.wireOp",EDGE,"E7");Q16=makeQuery(id+"F2.opShell","OFFSET_EDGE",EDGE,{"disambiguationData":[OSD([subQ1,subQ0]),TDD([makeQuery(id+"F1.opExtrude","CAP_EDGE",EDGE,{"disambiguationData":[OSD([subQ1,subQ0])],"isStart":false})]),OD(1.0)]});}
            var Q17;
            {var subQ0=sQuery(id+"F0.wireOp",EDGE,"E16");Q17=makeQuery(id+"F2.opShell","OFFSET_EDGE",EDGE,{"disambiguationData":[OSD([subQ0]),TDD([makeQuery(id+"F1.opExtrude","CAP_EDGE",EDGE,{"disambiguationData":[OSD([subQ0])],"isStart":false})])]});}
            var Q18;
            Q18=makeQuery(id+"F2.opShell","OFFSET_EDGE",EDGE,{"disambiguationData":[OSD([sQuery(id+"F0.wireOp",EDGE,"E14"),sQuery(id+"F0.wireOp",EDGE,"E16")])]});
            var Q19;
            Q19=makeQuery(id+"F2.opShell","TWEAK_EDGE",EDGE,{"derivedFrom":[makeQuery(id+"F1.opExtrude","SWEPT_FACE",FACE,{"disambiguationData":[OSD([sQuery(id+"F0.wireOp",EDGE,"E3.left")])]}),makeQuery(id+"F1.opExtrude","SWEPT_FACE",FACE,{"disambiguationData":[OSD([sQuery(id+"F0.wireOp",EDGE,"E7"),sQuery(id+"F0.wireOp",EDGE,"E14")])]})]});
            var Q20;
            Q20=makeQuery(id+"F2.opShell","TWEAK_EDGE",EDGE,{"derivedFrom":[makeQuery(id+"F1.opExtrude","SWEPT_FACE",FACE,{"disambiguationData":[OSD([sQuery(id+"F0.wireOp",EDGE,"E3.left")])]}),makeQuery(id+"F1.opExtrude","SWEPT_FACE",FACE,{"disambiguationData":[OSD([sQuery(id+"F0.wireOp",EDGE,"E16")])]})]});
            var Q21;
            Q21=makeQuery(id+"F4.opExtrude","CAP_EDGE",EDGE,{"disambiguationData":[OSD([sQuery(id+"F3.wireOp",EDGE,"E19.left")])],"isStart":false});
            var Q22;
            {var subQ0=sQuery(id+"F3.wireOp",EDGE,"E20.left");Q22=makeQuery(id+"F7.opFillet","BLEND_EDGE",EDGE,{"blendedFrom":[makeQuery(id+"F4.opExtrude","CAP_EDGE",EDGE,{"disambiguationData":[OSD([subQ0])],"isStart":true}),makeQuery(id+"F5.opFillet","SPLIT",FACE,{"disambiguationData":[OD(0.0)],"derivedFrom":makeQuery(id+"F4.opExtrude","CAP_FACE",FACE,{"disambiguationData":[OSD([sQuery(id+"F3.wireOp",EDGE,"E19.bottom"),sQuery(id+"F3.wireOp",EDGE,"E19.top"),sQuery(id+"F3.wireOp",EDGE,"E19.left"),sQuery(id+"F3.wireOp",EDGE,"E19.right"),sQuery(id+"F3.wireOp",EDGE,"E20.bottom"),sQuery(id+"F3.wireOp",EDGE,"E20.top"),subQ0,sQuery(id+"F3.wireOp",EDGE,"E20.right")])],"isStart":false})})],"blendedInto":[makeQuery(id+"F5.opFillet","SPLIT",FACE,{"disambiguationData":[OD(0.0)],"derivedFrom":makeQuery(id+"F4.opExtrude","CAP_FACE",FACE,{"disambiguationData":[OSD([sQuery(id+"F3.wireOp",EDGE,"E19.bottom"),sQuery(id+"F3.wireOp",EDGE,"E19.top"),sQuery(id+"F3.wireOp",EDGE,"E19.left"),sQuery(id+"F3.wireOp",EDGE,"E19.right"),sQuery(id+"F3.wireOp",EDGE,"E20.bottom"),sQuery(id+"F3.wireOp",EDGE,"E20.top"),subQ0,sQuery(id+"F3.wireOp",EDGE,"E20.right")])],"isStart":false})})]});}
            var Q23;
            Q23=makeQuery(id+"F4.opExtrude","CAP_EDGE",EDGE,{"disambiguationData":[OSD([sQuery(id+"F3.wireOp",EDGE,"E19.right")])],"isStart":false});
            var Q24;
            Q24=makeQuery(id+"F4.opExtrude","CAP_EDGE",EDGE,{"disambiguationData":[OSD([sQuery(id+"F3.wireOp",EDGE,"E20.right")])],"isStart":false});
            fillet(context, id + "F11", {"entities" : qUnion([Q0, Q1, Q2, Q3, Q4, Q5, Q6, Q7, Q8, Q9, Q10, Q11, Q12, Q13, Q14, Q15, Q16, Q17, Q18, Q19, Q20, Q21, Q22, Q23, Q24]), "radius" : 1 * mm, "tangentPropagation" : true, "allowEdgeOverflow" : false});
        }
        {
            var Q0;
            Q0=makeQuery(id+"F4.boolean.opBoolean","INTERSECT",EDGE,{"derivedFrom":[makeQuery(id+"F1.opExtrude","SWEPT_FACE",FACE,{"disambiguationData":[OSD([sQuery(id+"F0.wireOp",EDGE,"E14")])]}),makeQuery(id+"F4.opExtrude","SWEPT_FACE",FACE,{"disambiguationData":[OSD([sQuery(id+"F3.wireOp",EDGE,"E20.right")])]})]});
            fillet(context, id + "F12", {"entities" : qUnion([Q0]), "radius" : 13 * mm, "tangentPropagation" : true, "allowEdgeOverflow" : false});
        }
        {
            var Q0;
            {var subQ0=sQuery(id+"F0.wireOp",EDGE,"E16");var subQ1=sQuery(id+"F0.wireOp",EDGE,"E14");Q0=makeQuery(id+"F9.opFillet","BLEND_EDGE",EDGE,{"blendedFrom":[makeQuery(id+"F1.opExtrude","SWEPT_EDGE",EDGE,{"disambiguationData":[OSD([subQ1,subQ0])]}),makeQuery(id+"F4.boolean.opBoolean","SPLIT",FACE,{"disambiguationData":[TD([makeQuery(id+"F1.opExtrude","SWEPT_FACE",FACE,{"disambiguationData":[OSD([subQ0])]})])],"derivedFrom":makeQuery(id+"F1.opExtrude","SWEPT_FACE",FACE,{"disambiguationData":[OSD([subQ1])]})})],"blendedInto":[makeQuery(id+"F4.boolean.opBoolean","SPLIT",FACE,{"disambiguationData":[TD([makeQuery(id+"F1.opExtrude","SWEPT_FACE",FACE,{"disambiguationData":[OSD([subQ0])]})])],"derivedFrom":makeQuery(id+"F1.opExtrude","SWEPT_FACE",FACE,{"disambiguationData":[OSD([subQ1])]})})]});}
            var Q1;
            Q1=makeQuery(id+"F1.opExtrude","SWEPT_EDGE",EDGE,{"disambiguationData":[OSD([sQuery(id+"F0.wireOp",EDGE,"E0.bottom"),sQuery(id+"F0.wireOp",EDGE,"E3.left")])]});
            var Q2;
            Q2=makeQuery(id+"F1.opExtrude","SWEPT_EDGE",EDGE,{"disambiguationData":[OSD([sQuery(id+"F0.wireOp",EDGE,"E3.left"),sQuery(id+"F0.wireOp",EDGE,"E4.top"),sQuery(id+"F0.wireOp",EDGE,"E4.left")])]});
            var Q3;
            {var subQ0=sQuery(id+"F0.wireOp",EDGE,"E16");var subQ1=sQuery(id+"F0.wireOp",EDGE,"E14");Q3=makeQuery(id+"F10.opFillet","BLEND_EDGE",EDGE,{"blendedFrom":[makeQuery(id+"F1.opExtrude","CAP_EDGE",EDGE,{"disambiguationData":[OSD([subQ1])],"isStart":false}),makeQuery(id+"F4.boolean.opBoolean","SPLIT",FACE,{"disambiguationData":[TD([makeQuery(id+"F1.opExtrude","SWEPT_FACE",FACE,{"disambiguationData":[OSD([subQ0])]})])],"derivedFrom":makeQuery(id+"F1.opExtrude","SWEPT_FACE",FACE,{"disambiguationData":[OSD([subQ1])]})})],"blendedInto":[makeQuery(id+"F4.boolean.opBoolean","SPLIT",FACE,{"disambiguationData":[TD([makeQuery(id+"F1.opExtrude","SWEPT_FACE",FACE,{"disambiguationData":[OSD([subQ0])]})])],"derivedFrom":makeQuery(id+"F1.opExtrude","SWEPT_FACE",FACE,{"disambiguationData":[OSD([subQ1])]})})]});}
            var Q4;
            {var subQ0=sQuery(id+"F0.wireOp",EDGE,"E16");var subQ1=sQuery(id+"F0.wireOp",EDGE,"E14");Q4=makeQuery(id+"F10.opFillet","BLEND_EDGE",EDGE,{"blendedFrom":[makeQuery(id+"F1.opExtrude","CAP_EDGE",EDGE,{"disambiguationData":[OSD([subQ1])],"isStart":true}),makeQuery(id+"F4.boolean.opBoolean","SPLIT",FACE,{"disambiguationData":[TD([makeQuery(id+"F1.opExtrude","SWEPT_FACE",FACE,{"disambiguationData":[OSD([subQ0])]})])],"derivedFrom":makeQuery(id+"F1.opExtrude","SWEPT_FACE",FACE,{"disambiguationData":[OSD([subQ1])]})})],"blendedInto":[makeQuery(id+"F4.boolean.opBoolean","SPLIT",FACE,{"disambiguationData":[TD([makeQuery(id+"F1.opExtrude","SWEPT_FACE",FACE,{"disambiguationData":[OSD([subQ0])]})])],"derivedFrom":makeQuery(id+"F1.opExtrude","SWEPT_FACE",FACE,{"disambiguationData":[OSD([subQ1])]})})]});}
            var Q5;
            Q5=makeQuery(id+"F12.opFillet","BLEND_EDGE",EDGE,{"blendedFrom":[makeQuery(id+"F4.boolean.opBoolean","INTERSECT",EDGE,{"derivedFrom":[makeQuery(id+"F1.opExtrude","SWEPT_FACE",FACE,{"disambiguationData":[OSD([sQuery(id+"F0.wireOp",EDGE,"E14")])]}),makeQuery(id+"F4.opExtrude","SWEPT_FACE",FACE,{"disambiguationData":[OSD([sQuery(id+"F3.wireOp",EDGE,"E20.right")])]})]}),makeQuery(id+"F6.opFillet","BLEND_FACE",FACE,{"disambiguationData":[OSD([sQuery(id+"F3.wireOp",EDGE,"E20.top")])]})],"blendedInto":[makeQuery(id+"F6.opFillet","BLEND_FACE",FACE,{"disambiguationData":[OSD([sQuery(id+"F3.wireOp",EDGE,"E20.top")])]})]});
            var Q6;
            Q6=makeQuery(id+"F12.opFillet","BLEND_EDGE",EDGE,{"blendedFrom":[makeQuery(id+"F4.boolean.opBoolean","INTERSECT",EDGE,{"derivedFrom":[makeQuery(id+"F1.opExtrude","SWEPT_FACE",FACE,{"disambiguationData":[OSD([sQuery(id+"F0.wireOp",EDGE,"E14")])]}),makeQuery(id+"F4.opExtrude","SWEPT_FACE",FACE,{"disambiguationData":[OSD([sQuery(id+"F3.wireOp",EDGE,"E20.right")])]})]}),makeQuery(id+"F6.opFillet","BLEND_FACE",FACE,{"disambiguationData":[OSD([sQuery(id+"F3.wireOp",EDGE,"E20.bottom")])]})],"blendedInto":[makeQuery(id+"F6.opFillet","BLEND_FACE",FACE,{"disambiguationData":[OSD([sQuery(id+"F3.wireOp",EDGE,"E20.bottom")])]})]});
            var Q7;
            Q7=makeQuery(id+"F7.opFillet","BLEND_EDGE",EDGE,{"blendedFrom":[makeQuery(id+"F4.opExtrude","CAP_EDGE",EDGE,{"disambiguationData":[OSD([sQuery(id+"F3.wireOp",EDGE,"E20.left")])],"isStart":true}),makeQuery(id+"F6.opFillet","BLEND_FACE",FACE,{"disambiguationData":[OSD([sQuery(id+"F3.wireOp",EDGE,"E20.top")])]})],"blendedInto":[makeQuery(id+"F6.opFillet","BLEND_FACE",FACE,{"disambiguationData":[OSD([sQuery(id+"F3.wireOp",EDGE,"E20.top")])]})]});
            var Q8;
            Q8=makeQuery(id+"F7.opFillet","BLEND_EDGE",EDGE,{"blendedFrom":[makeQuery(id+"F4.opExtrude","CAP_EDGE",EDGE,{"disambiguationData":[OSD([sQuery(id+"F3.wireOp",EDGE,"E20.left")])],"isStart":true}),makeQuery(id+"F6.opFillet","BLEND_FACE",FACE,{"disambiguationData":[OSD([sQuery(id+"F3.wireOp",EDGE,"E20.bottom")])]})],"blendedInto":[makeQuery(id+"F6.opFillet","BLEND_FACE",FACE,{"disambiguationData":[OSD([sQuery(id+"F3.wireOp",EDGE,"E20.bottom")])]})]});
            var Q9;
            {var subQ0=sQuery(id+"F0.wireOp",EDGE,"E14");Q9=makeQuery(id+"F10.opFillet","BLEND_EDGE",EDGE,{"blendedFrom":[makeQuery(id+"F1.opExtrude","CAP_EDGE",EDGE,{"disambiguationData":[OSD([subQ0])],"isStart":true}),makeQuery(id+"F9.opFillet","BLEND_FACE",FACE,{"disambiguationData":[OSD([subQ0,sQuery(id+"F0.wireOp",EDGE,"E16")])]})],"blendedInto":[makeQuery(id+"F9.opFillet","BLEND_FACE",FACE,{"disambiguationData":[OSD([subQ0,sQuery(id+"F0.wireOp",EDGE,"E16")])]})]});}
            var Q10;
            {var subQ0=sQuery(id+"F0.wireOp",EDGE,"E16");Q10=makeQuery(id+"F9.opFillet","BLEND_EDGE",EDGE,{"blendedFrom":[makeQuery(id+"F1.opExtrude","CAP_EDGE",EDGE,{"disambiguationData":[OSD([subQ0])],"isStart":true}),makeQuery(id+"F1.opExtrude","SWEPT_EDGE",EDGE,{"disambiguationData":[OSD([sQuery(id+"F0.wireOp",EDGE,"E14"),subQ0])]})],"blendedInto":[]});}
            var Q11;
            {var subQ0=sQuery(id+"F0.wireOp",EDGE,"E16");Q11=makeQuery(id+"F10.opFillet","BLEND_EDGE",EDGE,{"blendedFrom":[makeQuery(id+"F1.opExtrude","CAP_EDGE",EDGE,{"disambiguationData":[OSD([sQuery(id+"F0.wireOp",EDGE,"E14")])],"isStart":true}),makeQuery(id+"F9.opFillet","BLEND_FACE",FACE,{"disambiguationData":[OSD([subQ0]),TDD([makeQuery(id+"F1.opExtrude","CAP_EDGE",EDGE,{"disambiguationData":[OSD([subQ0])],"isStart":true})])]})],"blendedInto":[makeQuery(id+"F9.opFillet","BLEND_FACE",FACE,{"disambiguationData":[OSD([subQ0]),TDD([makeQuery(id+"F1.opExtrude","CAP_EDGE",EDGE,{"disambiguationData":[OSD([subQ0])],"isStart":true})])]})]});}
            var Q12;
            {var subQ0=sQuery(id+"F0.wireOp",EDGE,"E16");Q12=makeQuery(id+"F10.opFillet","BLEND_EDGE",EDGE,{"blendedFrom":[makeQuery(id+"F1.opExtrude","CAP_EDGE",EDGE,{"disambiguationData":[OSD([sQuery(id+"F0.wireOp",EDGE,"E14")])],"isStart":false}),makeQuery(id+"F9.opFillet","BLEND_FACE",FACE,{"disambiguationData":[OSD([subQ0]),TDD([makeQuery(id+"F1.opExtrude","CAP_EDGE",EDGE,{"disambiguationData":[OSD([subQ0])],"isStart":false})])]})],"blendedInto":[makeQuery(id+"F9.opFillet","BLEND_FACE",FACE,{"disambiguationData":[OSD([subQ0]),TDD([makeQuery(id+"F1.opExtrude","CAP_EDGE",EDGE,{"disambiguationData":[OSD([subQ0])],"isStart":false})])]})]});}
            var Q13;
            {var subQ0=sQuery(id+"F0.wireOp",EDGE,"E14");Q13=makeQuery(id+"F10.opFillet","BLEND_EDGE",EDGE,{"blendedFrom":[makeQuery(id+"F1.opExtrude","CAP_EDGE",EDGE,{"disambiguationData":[OSD([subQ0])],"isStart":false}),makeQuery(id+"F9.opFillet","BLEND_FACE",FACE,{"disambiguationData":[OSD([subQ0,sQuery(id+"F0.wireOp",EDGE,"E16")])]})],"blendedInto":[makeQuery(id+"F9.opFillet","BLEND_FACE",FACE,{"disambiguationData":[OSD([subQ0,sQuery(id+"F0.wireOp",EDGE,"E16")])]})]});}
            var Q14;
            {var subQ0=sQuery(id+"F0.wireOp",EDGE,"E16");Q14=makeQuery(id+"F9.opFillet","BLEND_EDGE",EDGE,{"blendedFrom":[makeQuery(id+"F1.opExtrude","CAP_EDGE",EDGE,{"disambiguationData":[OSD([subQ0])],"isStart":false}),makeQuery(id+"F1.opExtrude","SWEPT_EDGE",EDGE,{"disambiguationData":[OSD([sQuery(id+"F0.wireOp",EDGE,"E14"),subQ0])]})],"blendedInto":[]});}
            var Q15;
            {var subQ0=sQuery(id+"F0.wireOp",EDGE,"E8");var subQ1=makeQuery(id+"F1.opExtrude","CAP_EDGE",EDGE,{"disambiguationData":[OSD([subQ0])],"isStart":false});Q15=makeQuery(id+"F10.opFillet","BLEND_EDGE",EDGE,{"blendedFrom":[makeQuery(id+"F9.opFillet","BLEND_EDGE",EDGE,{"blendedFrom":[subQ1,makeQuery(id+"F6.opFillet","BLEND_FACE",FACE,{"disambiguationData":[OSD([sQuery(id+"F3.wireOp",EDGE,"E20.bottom")])]})],"blendedInto":[makeQuery(id+"F6.opFillet","BLEND_FACE",FACE,{"disambiguationData":[OSD([sQuery(id+"F3.wireOp",EDGE,"E20.bottom")])]})]}),makeQuery(id+"F9.opFillet","BLEND_FACE",FACE,{"disambiguationData":[OSD([subQ0]),TDD([subQ1])]})],"blendedInto":[makeQuery(id+"F9.opFillet","BLEND_FACE",FACE,{"disambiguationData":[OSD([subQ0]),TDD([subQ1])]})]});}
            var Q16;
            {var subQ0=sQuery(id+"F0.wireOp",EDGE,"E8");Q16=makeQuery(id+"F9.opFillet","BLEND_EDGE",EDGE,{"blendedFrom":[makeQuery(id+"F1.opExtrude","CAP_EDGE",EDGE,{"disambiguationData":[OSD([subQ0])],"isStart":false}),makeQuery(id+"F1.opExtrude","SWEPT_EDGE",EDGE,{"disambiguationData":[OSD([sQuery(id+"F0.wireOp",EDGE,"E7"),subQ0,sQuery(id+"F0.wireOp",EDGE,"E11.top"),sQuery(id+"F0.wireOp",EDGE,"E12.top"),sQuery(id+"F0.wireOp",EDGE,"E11.right")])]})],"blendedInto":[]});}
            var Q17;
            {var subQ0=sQuery(id+"F0.wireOp",EDGE,"E8");var subQ1=makeQuery(id+"F1.opExtrude","CAP_EDGE",EDGE,{"disambiguationData":[OSD([subQ0])],"isStart":true});Q17=makeQuery(id+"F10.opFillet","BLEND_EDGE",EDGE,{"blendedFrom":[makeQuery(id+"F9.opFillet","BLEND_EDGE",EDGE,{"blendedFrom":[subQ1,makeQuery(id+"F6.opFillet","BLEND_FACE",FACE,{"disambiguationData":[OSD([sQuery(id+"F3.wireOp",EDGE,"E20.top")])]})],"blendedInto":[makeQuery(id+"F6.opFillet","BLEND_FACE",FACE,{"disambiguationData":[OSD([sQuery(id+"F3.wireOp",EDGE,"E20.top")])]})]}),makeQuery(id+"F9.opFillet","BLEND_FACE",FACE,{"disambiguationData":[OSD([subQ0]),TDD([subQ1])]})],"blendedInto":[makeQuery(id+"F9.opFillet","BLEND_FACE",FACE,{"disambiguationData":[OSD([subQ0]),TDD([subQ1])]})]});}
            var Q18;
            {var subQ0=sQuery(id+"F0.wireOp",EDGE,"E14");Q18=makeQuery(id+"F12.opFillet","BLEND_EDGE",EDGE,{"blendedFrom":[makeQuery(id+"F4.boolean.opBoolean","INTERSECT",EDGE,{"derivedFrom":[makeQuery(id+"F1.opExtrude","SWEPT_FACE",FACE,{"disambiguationData":[OSD([subQ0])]}),makeQuery(id+"F4.opExtrude","SWEPT_FACE",FACE,{"disambiguationData":[OSD([sQuery(id+"F3.wireOp",EDGE,"E20.right")])]})]}),makeQuery(id+"F9.opFillet","BLEND_FACE",FACE,{"disambiguationData":[OSD([subQ0,sQuery(id+"F0.wireOp",EDGE,"E16")])]})],"blendedInto":[makeQuery(id+"F9.opFillet","BLEND_FACE",FACE,{"disambiguationData":[OSD([subQ0,sQuery(id+"F0.wireOp",EDGE,"E16")])]})]});}
            fillet(context, id + "F13", {"entities" : qUnion([Q0, Q1, Q2, Q3, Q4, Q5, Q6, Q7, Q8, Q9, Q10, Q11, Q12, Q13, Q14, Q15, Q16, Q17, Q18]), "radius" : 0.5 * mm, "allowEdgeOverflow" : false});
        }
    });
